# Revit family: LeL Bright 1.0 316L
name_source: partatom
category: Lighting Fixtures
units: mm (PartAtom-declared; Revit-internal decimal feet)

## family parameters
Cut with Voids When Loaded = Yes
Host = Face
Light Source = No
Part Type = Normal
Room Calculation Point = No
Round Connector Dimension = Use Diameter
Shared = No

## types (4) — shared parameters
Accessories = WC5003 outer casing
Alimentazione = 0 V
Apparent Load = 2 VA
CCT = 3000 K
CRI = 80
Current = 1 A
Default Elevation = 1219 mm
Description = Outdoor Linear Profile
Finish = LeL Stainless Steel
IK = IK10
IP = IP68
Lamp = LED
Manufacturer = L&L Luce&Light
Model = CW10
Rated Power supply = 0 V
URL = https://www.lucelight.it
Wattage = 2 W
Weight = 0.48 kg
zero-valued in all types: Void offset

## per-type parameters (varying)
| type | Photometry |
| D diffuse 2W | CW10 Light source : Diffuse 2W |
| S 10° 2W | CW10 Light source : S 10° 2W |
| M 21° 2W | CW10 Light source : M 21° 2W |
| L 43° 2W | CW10 Light source : L 43° 2W |

## geometry (parser evidence)
native form markers: Sweep x3
no freeform markers — native parametric forms only
